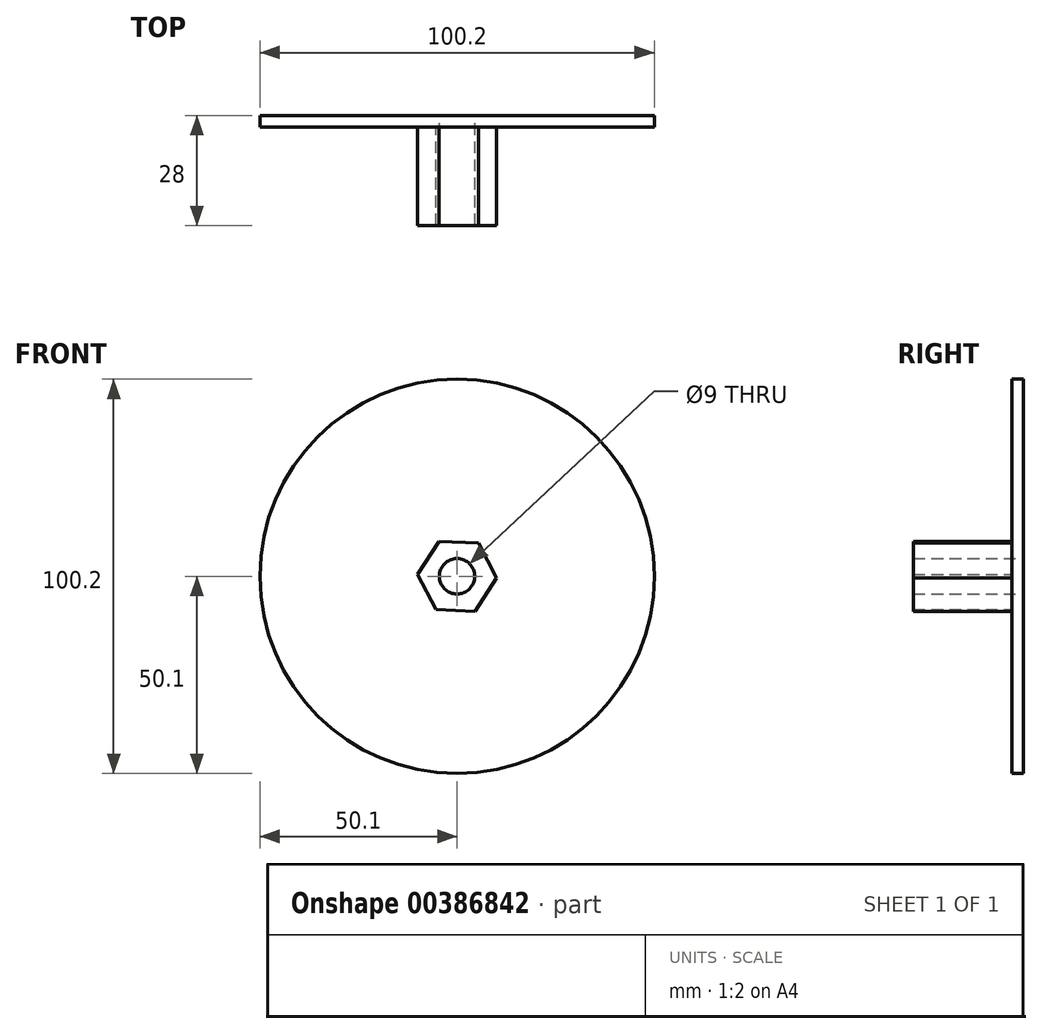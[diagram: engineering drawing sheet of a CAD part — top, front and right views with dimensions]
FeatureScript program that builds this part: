
annotation { "Feature Type Name" : "Feature", "Feature Type Description" : "" }
export const myFeature = defineFeature(function(context is Context, id is Id, definition is map)
    precondition{}
    {
        {
            var Q0;
            Q0=qCreatedBy(makeId("Front.planeOp"),FACE);
            var sketch = newSketch(context, id + "F0", { "sketchPlane" : qUnion([Q0])});
            skCircle(sketch, "E0", {"center": v(0, 0) * mm, "radius": 50.1 * mm});
            skCircle(sketch, "E1", {"center": v(0, 0) * mm, "radius": 4.5 * mm});
            skSolve(sketch);
        }
        {
            var Q0;
            Q0 = qSketchRegion(id + "F0", true);
            extrude(context, id + "F1", {"entities" : qUnion([Q0]), "depth" : 3 * mm});
        }
        {
            var Q0;
            Q0=makeQuery(id+"F1.opExtrude","CAP_FACE",FACE,{"disambiguationData":[OSD([sQuery(id+"F0.wireOp",EDGE,"E0"),sQuery(id+"F0.wireOp",EDGE,"E1")])],"isStart":false});
            var sketch = newSketch(context, id + "F2", { "sketchPlane" : qUnion([Q0])});
            skCircle(sketch, "E2", {"center": v(0, 0) * mm, "radius": 4.5 * mm});
            skCircle(sketch, "E3.cCircle", {"center": v(0, 0) * mm, "radius": 8.66 * mm, "construction": true});
            skLineSegment(sketch, "E3.0", {"start": v(-9.99, 0.48) * mm, "end": v(-4.58, 8.89) * mm});
            skLineSegment(sketch, "E3.1", {"start": v(-4.58, 8.89) * mm, "end": v(5.4, 8.41) * mm});
            skLineSegment(sketch, "E3.2", {"start": v(5.4, 8.41) * mm, "end": v(9.99, -0.48) * mm});
            skLineSegment(sketch, "E3.3", {"start": v(9.99, -0.48) * mm, "end": v(4.58, -8.89) * mm});
            skLineSegment(sketch, "E3.4", {"start": v(4.58, -8.89) * mm, "end": v(-5.4, -8.41) * mm});
            skLineSegment(sketch, "E3.5", {"start": v(-5.4, -8.41) * mm, "end": v(-9.99, 0.48) * mm});
            skPoint(sketch, "E3.0.midPoint", {"position": v(-7.28, 4.68) * mm});
            skSolve(sketch);
        }
        {
            var Q0;
            Q0 = qSketchRegion(id + "F2", true);
            extrude(context, id + "F3", {"entities" : qUnion([Q0]), "operationType" : NewBodyOperationType.ADD, "depth" : 25 * mm});
        }
    });
